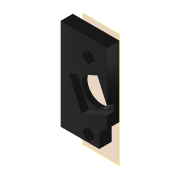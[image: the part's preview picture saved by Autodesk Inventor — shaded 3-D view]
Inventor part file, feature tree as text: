
AUTODESK INVENTOR PART (.ipt)
format: ipt  version: 2022 (Build 260153000, 153)  size: 581,120 bytes
history: native  units: mm
features: other x4, plane x2, extrude x2, chamfer x1, sketch x1, projected_geometry x1
ambient origin geometry x8: Origin, YZ Plane, XZ Plane, XY Plane, X Axis, Y Axis, Z Axis, Center Point
bodies: Volumenkörper1 (feature_tree)
feature tree (11):
  plane  "Arbeitsebene1"
  plane  "Arbeitsebene2"
  extrude  "Extrusion1"  Depth=8.0mm
  extrude  "Extrusion4"  Depth=1.5mm TaperAngle=0.0deg
  chamfer  "Fase2"  Distance=2.0mm
  sketch  "Skizze4"  dims[d0=6.0mm d1=8.0mm d2=1.5mm d3=0.0mm d10=2.0mm d11=3.2mm d12=20.0mm d13=3.2mm d14=19.0mm d15=8.2mm d40=8.8mm d41=19.896753mm d42=8.8mm d44=0.0mm d45=5.25mm d46=9.0mm d47=2.0mm d48=0.0mm d49=2.0mm d50=2.0mm d51=45.0deg d53=0.25mm]
  other  "Bild1"
  projected_geometry  "Projizierte Kontur3"
  other  "Assembly_Autofocus_ke400.iam"
  other  "00_KES_400_BlurayOPU:1"
  other  "00_KES400A_base:1"
